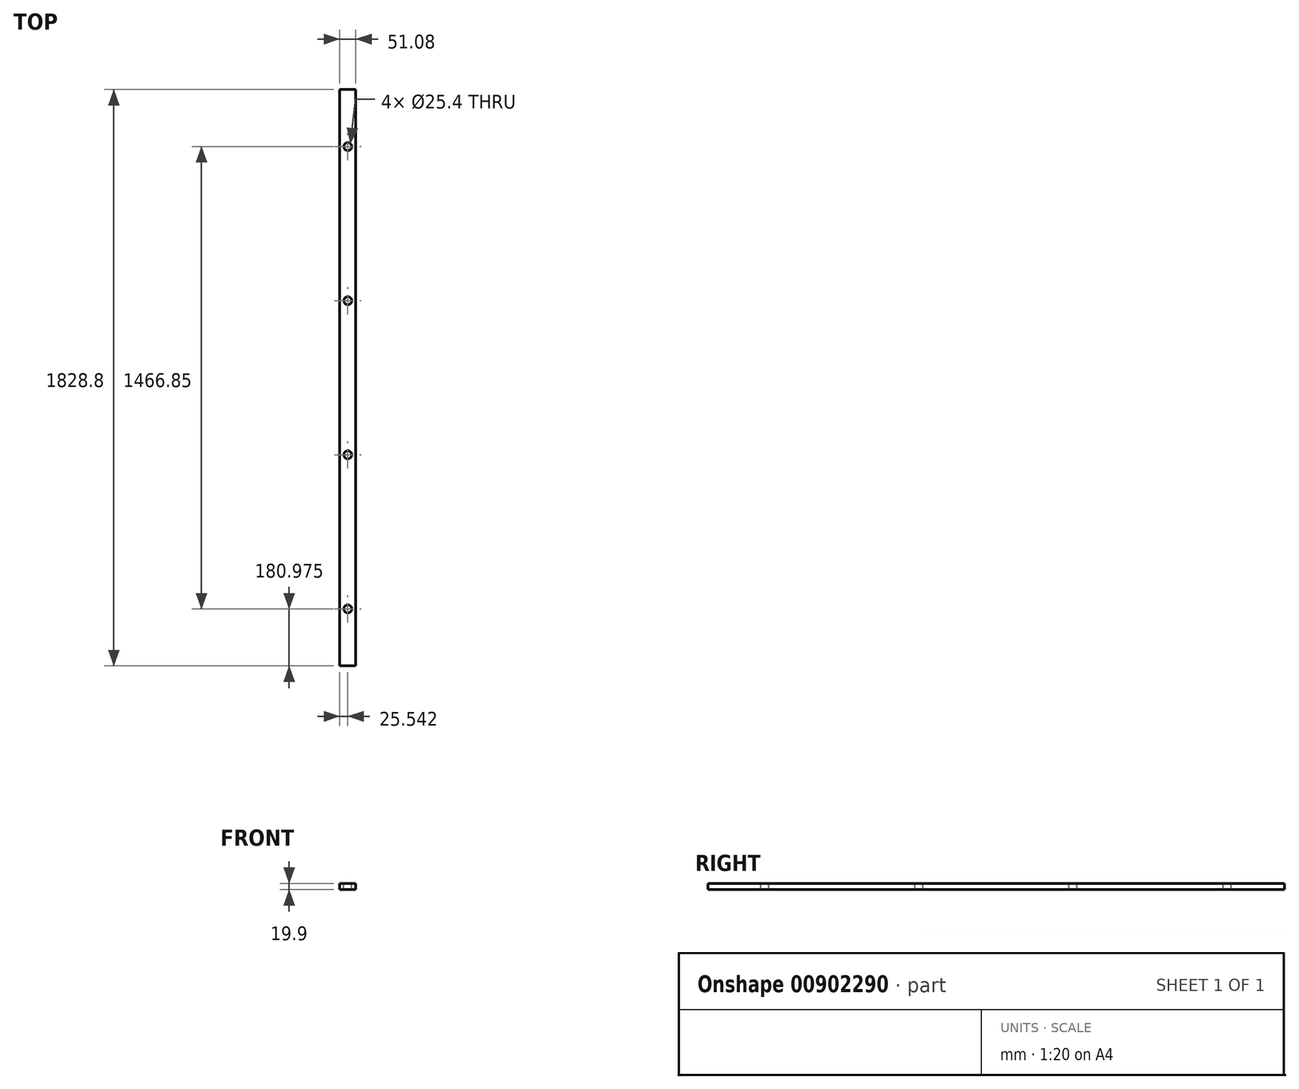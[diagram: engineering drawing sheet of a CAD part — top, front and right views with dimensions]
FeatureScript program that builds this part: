
annotation { "Feature Type Name" : "Feature", "Feature Type Description" : "" }
export const myFeature = defineFeature(function(context is Context, id is Id, definition is map)
    precondition{}
    {
        {
            var Q0;
            Q0=qCreatedBy(makeId("Front.planeOp"),FACE);
            var sketch = newSketch(context, id + "F0", { "sketchPlane" : qUnion([Q0])});
            skLineSegment(sketch, "E0.bottom", {"start": v(0, 0) * mm, "end": v(51.08, 0) * mm});
            skLineSegment(sketch, "E0.top", {"start": v(0, 19.9) * mm, "end": v(51.08, 19.9) * mm});
            skLineSegment(sketch, "E0.left", {"start": v(0, 0) * mm, "end": v(0, 19.9) * mm});
            skLineSegment(sketch, "E0.right", {"start": v(51.08, 0) * mm, "end": v(51.08, 19.9) * mm});
            skSolve(sketch);
        }
        {
            var Q0;
            Q0 = qSketchRegion(id + "F0", true);
            extrude(context, id + "F1", {"entities" : qUnion([Q0]), "depth" : 1828.8 * mm, "offsetDistance" : 25.4 * mm});
        }
        {
            var Q0;
            Q0=makeQuery(id+"F1.opExtrude","SWEPT_FACE",FACE,{"disambiguationData":[OSD([sQuery(id+"F0.wireOp",EDGE,"E0.top")])]});
            var sketch = newSketch(context, id + "F2", { "sketchPlane" : qUnion([Q0])});
            skLineSegment(sketch, "E1", {"start": v(25.54, 0) * mm, "end": v(25.54, -1828.8) * mm, "construction": true});
            skPoint(sketch, "E2", {"position": v(25.54, -180.98) * mm});
            skPoint(sketch, "E3", {"position": v(25.54, -669.93) * mm});
            skPoint(sketch, "E4", {"position": v(25.54, -1158.88) * mm});
            skCircle(sketch, "E5", {"center": v(25.54, -180.98) * mm, "radius": 12.7 * mm});
            skCircle(sketch, "E6", {"center": v(25.54, -669.93) * mm, "radius": 12.7 * mm});
            skCircle(sketch, "E7", {"center": v(25.54, -1158.88) * mm, "radius": 12.7 * mm});
            skPoint(sketch, "E8", {"position": v(25.54, -1647.83) * mm});
            skCircle(sketch, "E9", {"center": v(25.54, -1647.83) * mm, "radius": 12.7 * mm});
            skSolve(sketch);
        }
        {
            var Q0;
            Q0=makeQuery(id+"F2.imprint","IMPRINT",FACE,{"disambiguationData":[TD([[makeQuery(id+"F2.imprint","IMPRINT",EDGE,{"derivedFrom":sQuery(id+"F2.wireOp",EDGE,"TAggQsJy-u7Yl-vUHU-ZB36-nmfJ9lSESs9m")}),1.0]])]});
            var Q1;
            Q1=makeQuery(id+"F2.imprint","IMPRINT",FACE,{"disambiguationData":[TD([[makeQuery(id+"F2.imprint","IMPRINT",EDGE,{"derivedFrom":sQuery(id+"F2.wireOp",EDGE,"E7")}),1.0]])]});
            var Q2;
            Q2=makeQuery(id+"F2.imprint","IMPRINT",FACE,{"disambiguationData":[TD([[makeQuery(id+"F2.imprint","IMPRINT",EDGE,{"derivedFrom":sQuery(id+"F2.wireOp",EDGE,"E6")}),1.0]])]});
            var Q3;
            Q3=makeQuery(id+"F2.imprint","IMPRINT",FACE,{"disambiguationData":[TD([[makeQuery(id+"F2.imprint","IMPRINT",EDGE,{"derivedFrom":sQuery(id+"F2.wireOp",EDGE,"E5")}),1.0]])]});
            var Q4;
            Q4=makeQuery(id+"F2.imprint","IMPRINT",FACE,{"disambiguationData":[TD([[makeQuery(id+"F2.imprint","IMPRINT",EDGE,{"derivedFrom":sQuery(id+"F2.wireOp",EDGE,"E9")}),1.0]])]});
            extrude(context, id + "F3", {"entities" : qUnion([Q0, Q1, Q2, Q3, Q4]), "operationType" : NewBodyOperationType.REMOVE, "endBound" : BoundingType.UP_TO_NEXT, "oppositeDirection" : true, "depth" : 25.4 * mm, "offsetDistance" : 25.4 * mm});
        }
    });
